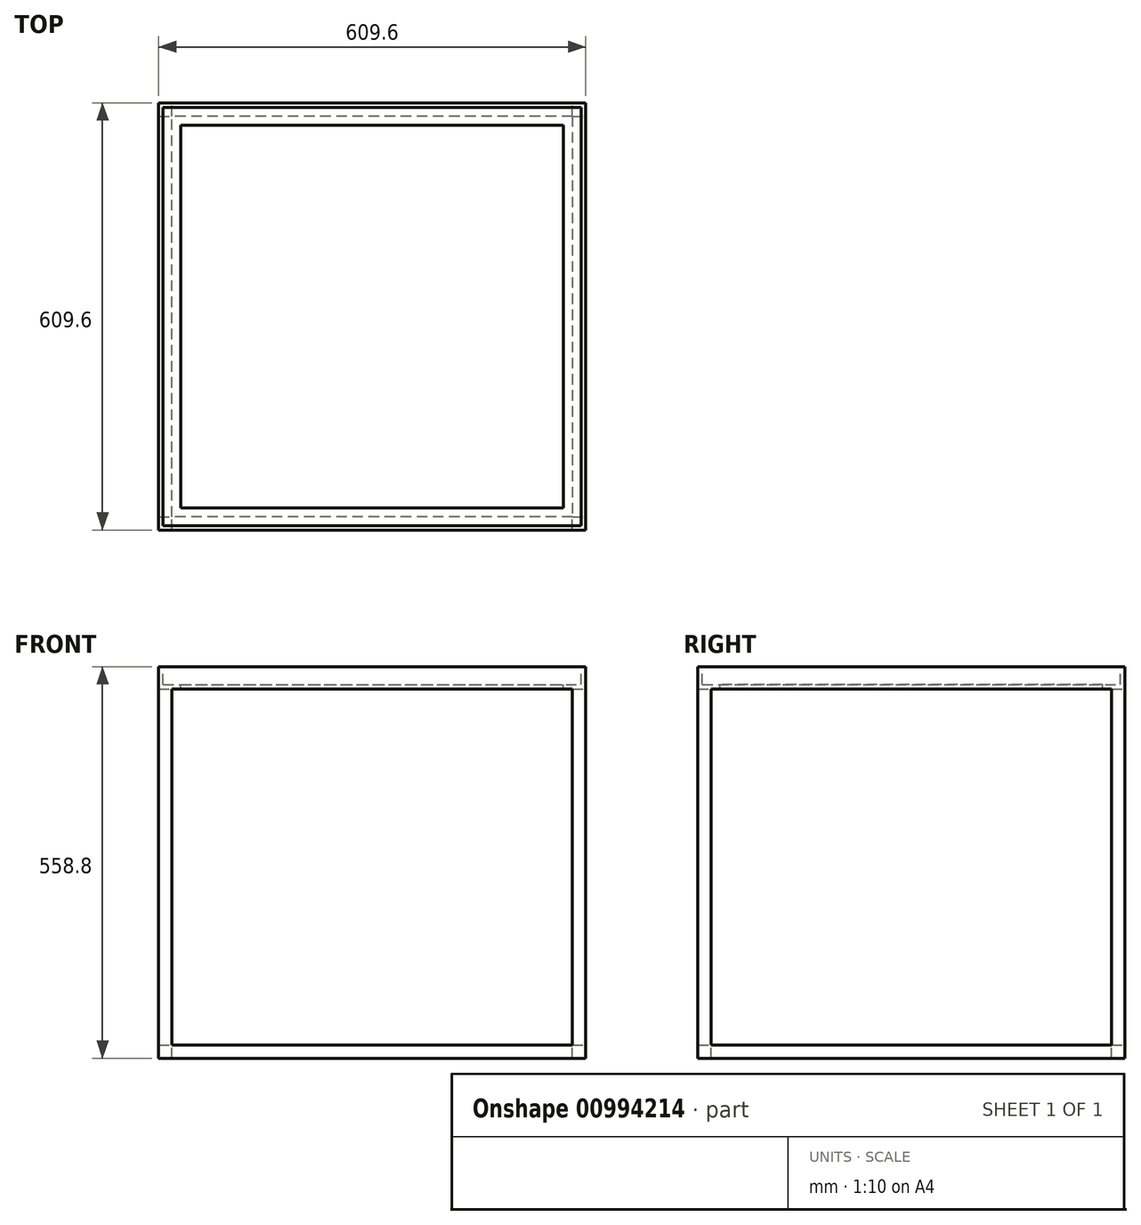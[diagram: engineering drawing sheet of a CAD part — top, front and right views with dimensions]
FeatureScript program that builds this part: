
annotation { "Feature Type Name" : "Feature", "Feature Type Description" : "" }
export const myFeature = defineFeature(function(context is Context, id is Id, definition is map)
    precondition{}
    {
        {
            var Q0;
            Q0=qCreatedBy(makeId("Front.planeOp"),FACE);
            var sketch = newSketch(context, id + "F0", { "sketchPlane" : qUnion([Q0])});
            skLineSegment(sketch, "E0.bottom", {"start": v(0, 0) * mm, "end": v(609.6, 0) * mm});
            skLineSegment(sketch, "E0.top", {"start": v(0, 558.8) * mm, "end": v(609.6, 558.8) * mm});
            skLineSegment(sketch, "E0.left", {"start": v(0, 0) * mm, "end": v(0, 558.8) * mm});
            skLineSegment(sketch, "E0.right", {"start": v(609.6, 0) * mm, "end": v(609.6, 558.8) * mm});
            skLineSegment(sketch, "E1", {"start": v(19.05, 527.05) * mm, "end": v(19.05, 19.05) * mm});
            skLineSegment(sketch, "E2", {"start": v(19.05, 19.05) * mm, "end": v(590.55, 19.05) * mm});
            skLineSegment(sketch, "E3", {"start": v(590.55, 19.05) * mm, "end": v(590.55, 527.05) * mm});
            skLineSegment(sketch, "E4", {"start": v(590.55, 527.05) * mm, "end": v(19.05, 527.05) * mm});
            skSolve(sketch);
        }
        {
            var Q0;
            Q0 = qSketchRegion(id + "F0", true);
            extrude(context, id + "F1", {"entities" : qUnion([Q0]), "depth" : 609.6 * mm, "offsetDistance" : 25.4 * mm});
        }
        {
            var Q0;
            Q0=makeQuery(id+"F1.opExtrude","SWEPT_FACE",FACE,{"disambiguationData":[OSD([sQuery(id+"F0.wireOp",EDGE,"E0.right")])]});
            var sketch = newSketch(context, id + "F2", { "sketchPlane" : qUnion([Q0])});
            skLineSegment(sketch, "E5.bottom", {"start": v(-590.55, 527.05) * mm, "end": v(-19.05, 527.05) * mm});
            skLineSegment(sketch, "E5.top", {"start": v(-590.55, 19.05) * mm, "end": v(-19.05, 19.05) * mm});
            skLineSegment(sketch, "E5.left", {"start": v(-590.55, 527.05) * mm, "end": v(-590.55, 19.05) * mm});
            skLineSegment(sketch, "E5.right", {"start": v(-19.05, 527.05) * mm, "end": v(-19.05, 19.05) * mm});
            skSolve(sketch);
        }
        {
            var Q0;
            Q0 = qSketchRegion(id + "F2", true);
            extrude(context, id + "F3", {"entities" : qUnion([Q0]), "operationType" : NewBodyOperationType.REMOVE, "endBound" : BoundingType.THROUGH_ALL, "oppositeDirection" : true, "depth" : 25.4 * mm, "offsetDistance" : 25.4 * mm});
        }
        {
            var Q0;
            Q0=makeQuery(id+"F1.opExtrude","SWEPT_FACE",FACE,{"disambiguationData":[OSD([sQuery(id+"F0.wireOp",EDGE,"E0.top")])]});
            var sketch = newSketch(context, id + "F4", { "sketchPlane" : qUnion([Q0])});
            skLineSegment(sketch, "E6.bottom", {"start": v(6.35, -603.25) * mm, "end": v(603.25, -603.25) * mm});
            skLineSegment(sketch, "E6.top", {"start": v(6.35, -6.35) * mm, "end": v(603.25, -6.35) * mm});
            skLineSegment(sketch, "E6.left", {"start": v(6.35, -603.25) * mm, "end": v(6.35, -6.35) * mm});
            skLineSegment(sketch, "E6.right", {"start": v(603.25, -603.25) * mm, "end": v(603.25, -6.35) * mm});
            skSolve(sketch);
        }
        {
            var Q0;
            Q0 = qSketchRegion(id + "F4", true);
            extrude(context, id + "F5", {"entities" : qUnion([Q0]), "operationType" : NewBodyOperationType.REMOVE, "oppositeDirection" : true, "depth" : 25.4 * mm, "offsetDistance" : 25.4 * mm});
        }
        {
            var Q0;
            Q0=makeQuery(id+"F5.boolean.opBoolean","COPY",FACE,{"derivedFrom":makeQuery(id+"F5.opExtrude","CAP_FACE",FACE,{"disambiguationData":[OSD([sQuery(id+"F4.wireOp",EDGE,"E6.bottom"),sQuery(id+"F4.wireOp",EDGE,"E6.top"),sQuery(id+"F4.wireOp",EDGE,"E6.left"),sQuery(id+"F4.wireOp",EDGE,"E6.right")])],"isStart":false})});
            var sketch = newSketch(context, id + "F6", { "sketchPlane" : qUnion([Q0])});
            skLineSegment(sketch, "E7.bottom", {"start": v(31.75, -31.75) * mm, "end": v(577.85, -31.75) * mm});
            skLineSegment(sketch, "E7.top", {"start": v(31.75, -577.85) * mm, "end": v(577.85, -577.85) * mm});
            skLineSegment(sketch, "E7.left", {"start": v(31.75, -31.75) * mm, "end": v(31.75, -577.85) * mm});
            skLineSegment(sketch, "E7.right", {"start": v(577.85, -31.75) * mm, "end": v(577.85, -577.85) * mm});
            skSolve(sketch);
        }
        {
            var Q0;
            Q0 = qSketchRegion(id + "F6", true);
            extrude(context, id + "F7", {"entities" : qUnion([Q0]), "operationType" : NewBodyOperationType.REMOVE, "endBound" : BoundingType.UP_TO_NEXT, "oppositeDirection" : true, "depth" : 25.4 * mm, "offsetDistance" : 25.4 * mm});
        }
        {
            var Q0;
            Q0=makeQuery(id+"F3.boolean.opBoolean","MERGE",FACE,{"derivedFrom":[makeQuery(id+"F1.opExtrude","SWEPT_FACE",FACE,{"disambiguationData":[OSD([sQuery(id+"F0.wireOp",EDGE,"E2")])]})],"fromTools":[makeQuery(id+"F3.opExtrude","SWEPT_FACE",FACE,{"disambiguationData":[OSD([sQuery(id+"F2.wireOp",EDGE,"E5.top")])]})]});
            var sketch = newSketch(context, id + "F8", { "sketchPlane" : qUnion([Q0])});
            skLineSegment(sketch, "E8.bottom", {"start": v(590.55, -19.05) * mm, "end": v(19.05, -19.05) * mm});
            skLineSegment(sketch, "E8.top", {"start": v(590.55, -590.55) * mm, "end": v(19.05, -590.55) * mm});
            skLineSegment(sketch, "E8.left", {"start": v(590.55, -19.05) * mm, "end": v(590.55, -590.55) * mm});
            skLineSegment(sketch, "E8.right", {"start": v(19.05, -19.05) * mm, "end": v(19.05, -590.55) * mm});
            skSolve(sketch);
        }
        {
            var Q0;
            Q0 = qSketchRegion(id + "F8", true);
            extrude(context, id + "F9", {"entities" : qUnion([Q0]), "operationType" : NewBodyOperationType.REMOVE, "endBound" : BoundingType.UP_TO_NEXT, "oppositeDirection" : true, "depth" : 25.4 * mm, "offsetDistance" : 25.4 * mm});
        }
    });
